# Revit family: Lüftungsrohrschelle Doppio, M 8-M10, DN224-630, Gummi
name_source: partatom
category: HLS-Bauteile
revit_build: Autodesk Revit 2017 (Build: 20190507_1515(x64)
units: mm (PartAtom-declared; Revit-internal decimal feet)

## family parameters
Arbeitsebenenbasiert = Ja
Beim Laden mit Abzugskörper schneiden = Nein
Bemaßung runder Anschluss = Durchmesser verwenden
Gemeinsam genutzt = Ja
Immer vertikal = Nein
Raumberechnungspunkt = Nein
Teiletyp = Normal

## types (12) — shared parameters
Anschluss = M8/M10
Bauart = zweiteilig
Baustoffklasse = B2
DS = 5 mm  [stored 0.0164042 ft]
DVS = 7 mm  [stored 0.0229659 ft]
Dämmstärke = 5 mm  [stored 0.0164042 ft]
Fabrikat = MEFA
Farbe Schalldämmeinlage = schwarz
Gesamthöhe Dämmung = 8 mm  [stored 0.0262467 ft]
HGA = 17 mm
MB = 25 mm  [stored 0.082021 ft]
Material = Stahl
Material Schalldämmeinlage = TPE
Mengeneinheit = St
Rohraußendurchmesser Zoll = Zoll
Schalldämmeinlage = Gummi
Verschluss = ohne Rastverschluss
Verschluss-Schraube = M8
Vorgabe-Ansicht = 1219 mm
max. Temperaturbeständigkeit = 100 °C
max. zul. Last horizontal = 0.00 kN
max. zul. Last vertikal = 0.00 kN
zero-valued in all types: AB, L1, Stärke Material, max. Rohraußendurchmesser, min. Rohraußendurchmesser

## per-type parameters (varying)
- Lüftungsrohrschelle Doppio, M8/M10, DN224, Gummi: A=24 mm  [stored 0.0787402 ft]; Anschlußhöhe=24 mm; Artikelnummer=0449224; B=272 mm; D=226 mm  [stored 0.74147 ft]; D0=235 mm; DF1=18 mm  [stored 0.0590551 ft]; DF2=48 mm  [stored 0.15748 ft]; DN=224 mm  [stored 0.734908 ft]; EAN=4250928411013; Gewicht=0.39 kg; Gewicht pro Bauteil=0.39 kg; H=258 mm; Höhe=258 mm; Kurztext1=Lüftungsschelle Doppio 25x1,5; Kurztext2=DN 224 M8/M10 TPE; MD=2 mm  [stored 0.00656168 ft]; Materialmaße=25x1,5 mm; Nennweite DN Rohr=224 mm  [stored 0.734908 ft]; R=118 mm; RM=119 mm; Rohraußendurchmesser=227 mm  [stored 0.744751 ft]; S=255 mm; Sicke=1 mm  [stored 0.00328084 ft]; vpe=10 St
- Lüftungsrohrschelle Doppio, M8/M10, DN250, Gummi: A=24 mm  [stored 0.0787402 ft]; Anschlußhöhe=24 mm; Artikelnummer=0449250; B=298 mm; D=252 mm  [stored 0.826772 ft]; D0=261 mm; DF1=18 mm  [stored 0.0590551 ft]; DF2=48 mm  [stored 0.15748 ft]; DN=250 mm  [stored 0.82021 ft]; EAN=4250928411020; Gewicht=0.43 kg; Gewicht pro Bauteil=0.43 kg; H=284 mm; Höhe=284 mm; Kurztext1=Lüftungsschelle Doppio 25x1,5; Kurztext2=DN 250 M8/M10 TPE; MD=2 mm  [stored 0.00656168 ft]; Materialmaße=25x1,5 mm; Nennweite DN Rohr=250 mm  [stored 0.82021 ft]; R=131 mm; RM=132 mm; Rohraußendurchmesser=253 mm  [stored 0.830052 ft]; S=281 mm; Sicke=1 mm  [stored 0.00328084 ft]; vpe=10 St
- Lüftungsrohrschelle Doppio, M8/M10, DN280, Gummi: A=24 mm  [stored 0.0787402 ft]; Anschlußhöhe=24 mm; Artikelnummer=0449280; B=328 mm; D=282 mm; D0=291 mm; DF1=18 mm  [stored 0.0590551 ft]; DF2=48 mm  [stored 0.15748 ft]; DN=280 mm; EAN=4250928411037; Gewicht=0.47 kg; Gewicht pro Bauteil=0.47 kg; H=314 mm; Höhe=314 mm; Kurztext1=Lüftungsschelle Doppio 25x1,5; Kurztext2=DN 280 M8/M10 TPE; MD=2 mm  [stored 0.00656168 ft]; Materialmaße=25x1,5 mm; Nennweite DN Rohr=280 mm; R=146 mm; RM=147 mm  [stored 0.482283 ft]; Rohraußendurchmesser=283 mm; S=311 mm; Sicke=1 mm  [stored 0.00328084 ft]; vpe=10 St
- Lüftungsrohrschelle Doppio, M8/M10, DN300, Gummi: A=24 mm  [stored 0.0787402 ft]; Anschlußhöhe=24 mm; Artikelnummer=0449300; B=348 mm; D=304 mm; D0=313 mm; DF1=18 mm  [stored 0.0590551 ft]; DF2=48 mm  [stored 0.15748 ft]; DN=300 mm; EAN=4250928411044; Gewicht=0.50 kg; Gewicht pro Bauteil=0.50 kg; H=336 mm; Höhe=336 mm; Kurztext1=Lüftungsschelle Doppio 25x1,5; Kurztext2=DN 300 M8/M10 TPE; MD=2 mm  [stored 0.00656168 ft]; Materialmaße=25x1,5 mm; Nennweite DN Rohr=300 mm; R=157 mm; RM=158 mm  [stored 0.518373 ft]; Rohraußendurchmesser=304 mm; S=333 mm; Sicke=1 mm  [stored 0.00328084 ft]; vpe=10 St
- Lüftungsrohrschelle Doppio, M8/M10, DN315, Gummi: A=24 mm  [stored 0.0787402 ft]; Anschlußhöhe=24 mm; Artikelnummer=0449315; B=363 mm; D=319 mm; D0=328 mm; DF1=18 mm  [stored 0.0590551 ft]; DF2=48 mm  [stored 0.15748 ft]; DN=315 mm; EAN=4250928411051; Gewicht=0.52 kg; Gewicht pro Bauteil=0.52 kg; H=351 mm; Höhe=351 mm; Kurztext1=Lüftungsschelle Doppio 25x1,5; Kurztext2=DN 315 M8/M10 TPE; MD=2 mm  [stored 0.00656168 ft]; Materialmaße=25x1,5 mm; Nennweite DN Rohr=315 mm; R=164 mm  [stored 0.538058 ft]; RM=166 mm; Rohraußendurchmesser=319 mm; S=348 mm; Sicke=1 mm  [stored 0.00328084 ft]; vpe=10 St
- Lüftungsrohrschelle Doppio, M8/M10, DN355, Gummi: A=24 mm  [stored 0.0787402 ft]; Anschlußhöhe=24 mm; Artikelnummer=0449355; B=432 mm; D=359 mm; D0=368 mm; DF1=24 mm  [stored 0.0787402 ft]; DF2=77 mm  [stored 0.252625 ft]; DN=355 mm; EAN=4250928411068; Gewicht=0.56 kg; Gewicht pro Bauteil=0.56 kg; H=391 mm; Höhe=391 mm; Kurztext1=Lüftungsschelle Doppio 25x1,5; Kurztext2=DN 355 M8/M10 TPE; MD=2 mm  [stored 0.00656168 ft]; Materialmaße=25x1,5 mm; Nennweite DN Rohr=355 mm; R=184 mm  [stored 0.603675 ft]; RM=186 mm; Rohraußendurchmesser=359 mm; S=394 mm; Sicke=1 mm  [stored 0.00328084 ft]; vpe=5 St
- Lüftungsrohrschelle Doppio, M8/M10, DN400, Gummi: A=24 mm  [stored 0.0787402 ft]; Anschlußhöhe=24 mm; Artikelnummer=0449400; B=477 mm; D=404 mm; D0=413 mm; DF1=24 mm  [stored 0.0787402 ft]; DF2=77 mm  [stored 0.252625 ft]; DN=400 mm; EAN=4250928411075; Gewicht=0.63 kg; Gewicht pro Bauteil=0.63 kg; H=436 mm; Höhe=436 mm; Kurztext1=Lüftungsschelle Doppio 25x1,5; Kurztext2=DN 400 M8/M10 TPE; MD=2 mm  [stored 0.00656168 ft]; Materialmaße=25x1,5 mm; Nennweite DN Rohr=400 mm; R=207 mm; RM=208 mm  [stored 0.682415 ft]; Rohraußendurchmesser=404 mm; S=439 mm; Sicke=1 mm  [stored 0.00328084 ft]; vpe=5 St
- Lüftungsrohrschelle Doppio, M8/M10, DN450, Gummi: A=24 mm  [stored 0.0787402 ft]; Anschlußhöhe=24 mm; Artikelnummer=0449450; B=527 mm; D=454 mm; D0=463 mm; DF1=24 mm  [stored 0.0787402 ft]; DF2=77 mm  [stored 0.252625 ft]; DN=450 mm; EAN=4250928411082; Gewicht=0.70 kg; Gewicht pro Bauteil=0.70 kg; H=486 mm; Höhe=486 mm; Kurztext1=Lüftungsschelle Doppio 25x1,5; Kurztext2=DN 450 M8/M10 TPE; MD=2 mm  [stored 0.00656168 ft]; Materialmaße=25x1,5 mm; Nennweite DN Rohr=450 mm; R=232 mm; RM=233 mm  [stored 0.764436 ft]; Rohraußendurchmesser=454 mm; S=489 mm; Sicke=1 mm  [stored 0.00328084 ft]; vpe=5 St
- Lüftungsrohrschelle Doppio, M8/M10, DN500, Gummi: A=26 mm; Anschlußhöhe=26 mm; Artikelnummer=0449500; B=578 mm; D=504 mm; D0=513 mm; DF1=24 mm  [stored 0.0787402 ft]; DF2=78 mm  [stored 0.255906 ft]; DN=500 mm; EAN=4250928411099; Gewicht=1.10 kg; Gewicht pro Bauteil=1.10 kg; H=538 mm; Höhe=538 mm; Kurztext1=Lüftungsschelle Doppio 25x2,5; Kurztext2=DN 500 M8/M10 TPE; MD=3 mm  [stored 0.00984252 ft]; Materialmaße=25x2,5 mm; Nennweite DN Rohr=500 mm; R=257 mm; RM=259 mm; Rohraußendurchmesser=504 mm; S=541 mm; Sicke=2 mm  [stored 0.00656168 ft]; vpe=1 St
- Lüftungsrohrschelle Doppio, M8/M10, DN560, Gummi: A=26 mm; Anschlußhöhe=26 mm; Artikelnummer=0449560; B=638 mm; D=564 mm; D0=573 mm; DF1=24 mm  [stored 0.0787402 ft]; DF2=78 mm  [stored 0.255906 ft]; DN=560 mm; EAN=4250928411112; Gewicht=1.22 kg; Gewicht pro Bauteil=1.22 kg; H=598 mm; Höhe=598 mm; Kurztext1=Lüftungsschelle Doppio 25x2,5; Kurztext2=DN 560 M8/M10 TPE; MD=3 mm  [stored 0.00984252 ft]; Materialmaße=25x2,5 mm; Nennweite DN Rohr=560 mm; R=287 mm; RM=289 mm; Rohraußendurchmesser=564 mm; S=601 mm; Sicke=2 mm  [stored 0.00656168 ft]; vpe=1 St
- Lüftungsrohrschelle Doppio, M8/M10, DN600, Gummi: A=26 mm; Anschlußhöhe=26 mm; Artikelnummer=0449600; B=678 mm; D=604 mm; D0=613 mm; DF1=24 mm  [stored 0.0787402 ft]; DF2=78 mm  [stored 0.255906 ft]; DN=600 mm; EAN=4250928411136; Gewicht=1.30 kg; Gewicht pro Bauteil=1.30 kg; H=638 mm; Höhe=638 mm; Kurztext1=Lüftungsschelle Doppio 25x2,5; Kurztext2=DN 600 M8/M10 TPE; MD=3 mm  [stored 0.00984252 ft]; Materialmaße=25x2,5 mm; Nennweite DN Rohr=600 mm; R=307 mm; RM=309 mm; Rohraußendurchmesser=605 mm; S=641 mm; Sicke=2 mm  [stored 0.00656168 ft]; vpe=1 St
- Lüftungsrohrschelle Doppio, M8/M10, DN630, Gummi: A=26 mm; Anschlußhöhe=26 mm; Artikelnummer=0449630; B=710 mm; D=637 mm; D0=646 mm; DF1=24 mm  [stored 0.0787402 ft]; DF2=80 mm  [stored 0.262467 ft]; DN=630 mm; EAN=4250928411150; Gewicht=1.36 kg; Gewicht pro Bauteil=1.36 kg; H=671 mm; Höhe=671 mm; Kurztext1=Lüftungsschelle Doppio 25x2,5; Kurztext2=DN 630 M8/M10 TPE; MD=3 mm  [stored 0.00984252 ft]; Materialmaße=25x2,5 mm; Nennweite DN Rohr=630 mm; R=323 mm; RM=326 mm; Rohraußendurchmesser=635 mm; S=674 mm; Sicke=2 mm  [stored 0.00656168 ft]; vpe=1 St

note: [stored X ft] marks values corroborated as IEEE doubles in the binary element streams (Revit-internal decimal feet)

## geometry (parser evidence)
native form markers: Sweep x9
no freeform markers — native parametric forms only
